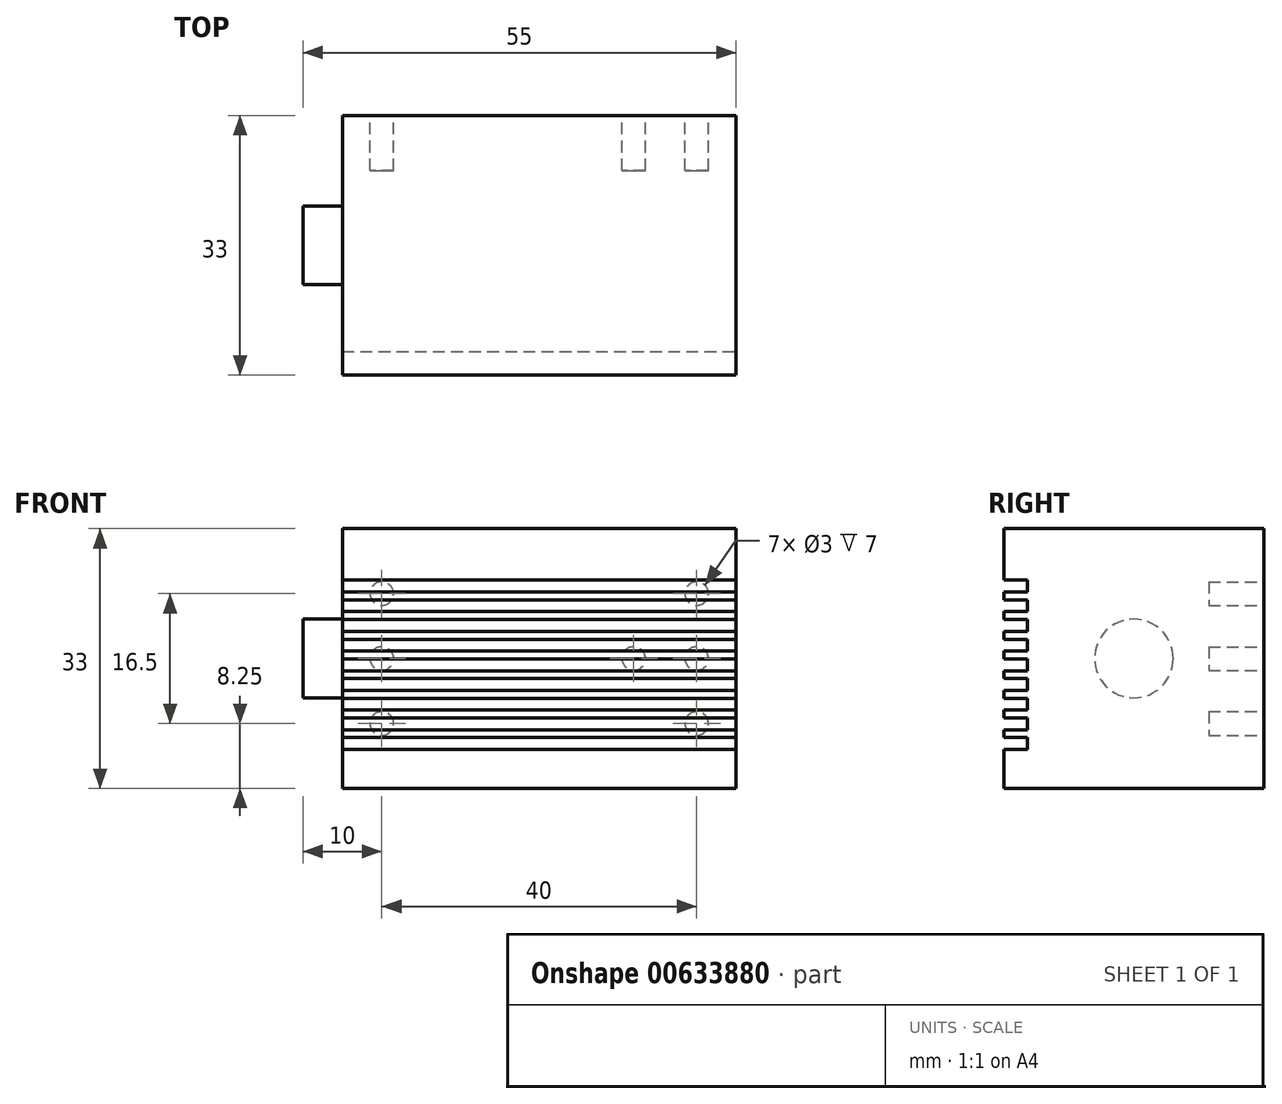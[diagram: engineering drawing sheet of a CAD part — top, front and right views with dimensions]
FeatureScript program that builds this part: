
annotation { "Feature Type Name" : "Feature", "Feature Type Description" : "" }
export const myFeature = defineFeature(function(context is Context, id is Id, definition is map)
    precondition{}
    {
        {
            var Q0;
            Q0=qCreatedBy(makeId("Top.planeOp"),FACE);
            var sketch = newSketch(context, id + "F0", { "sketchPlane" : qUnion([Q0])});
            skLineSegment(sketch, "E0.bottom", {"start": v(25, -16.5) * mm, "end": v(-25, -16.5) * mm});
            skLineSegment(sketch, "E0.top", {"start": v(25, 16.5) * mm, "end": v(-25, 16.5) * mm});
            skLineSegment(sketch, "E0.left", {"start": v(25, -16.5) * mm, "end": v(25, 16.5) * mm});
            skLineSegment(sketch, "E0.right", {"start": v(-25, -16.5) * mm, "end": v(-25, 16.5) * mm});
            skPoint(sketch, "E0.middle", {"position": v(0, 0) * mm});
            skSolve(sketch);
        }
        {
            var Q0;
            Q0=makeQuery(id+"F0.imprint","IMPRINT",FACE,{"disambiguationData":[TD([[makeQuery(id+"F0.imprint","IMPRINT",EDGE,{"derivedFrom":sQuery(id+"F0.wireOp",EDGE,"E0.bottom")}),-1.0]])]});
            extrude(context, id + "F1", {"entities" : qUnion([Q0]), "depth" : 33 * mm, "offsetDistance" : 25 * mm});
        }
        {
            var Q0;
            Q0=makeQuery(id+"F1.opExtrude","SWEPT_FACE",FACE,{"disambiguationData":[OSD([sQuery(id+"F0.wireOp",EDGE,"E0.left")])]});
            var sketch = newSketch(context, id + "F2", { "sketchPlane" : qUnion([Q0])});
            skLineSegment(sketch, "E1.bottom", {"start": v(-13.5, 24.95) * mm, "end": v(-19.5, 24.95) * mm});
            skLineSegment(sketch, "E1.top", {"start": v(-13.5, 26.45) * mm, "end": v(-19.5, 26.45) * mm});
            skLineSegment(sketch, "E1.left", {"start": v(-13.5, 24.95) * mm, "end": v(-13.5, 26.45) * mm});
            skLineSegment(sketch, "E1.right", {"start": v(-19.5, 24.95) * mm, "end": v(-19.5, 26.45) * mm});
            skPoint(sketch, "E1.middle", {"position": v(-16.5, 25.7) * mm});
            skPoint(sketch, "E2.0.1.0", {"position": v(-16.5, 23.2) * mm});
            skLineSegment(sketch, "E2.0.1.1", {"start": v(-13.5, 23.95) * mm, "end": v(-19.5, 23.95) * mm});
            skLineSegment(sketch, "E2.0.1.2", {"start": v(-13.5, 22.45) * mm, "end": v(-19.5, 22.45) * mm});
            skLineSegment(sketch, "E2.0.1.3", {"start": v(-19.5, 22.45) * mm, "end": v(-19.5, 23.95) * mm});
            skLineSegment(sketch, "E2.0.1.4", {"start": v(-13.5, 22.45) * mm, "end": v(-13.5, 23.95) * mm});
            skPoint(sketch, "E2.0.2.0", {"position": v(-16.5, 20.7) * mm});
            skLineSegment(sketch, "E2.0.2.1", {"start": v(-13.5, 21.45) * mm, "end": v(-19.5, 21.45) * mm});
            skLineSegment(sketch, "E2.0.2.2", {"start": v(-13.5, 19.95) * mm, "end": v(-19.5, 19.95) * mm});
            skLineSegment(sketch, "E2.0.2.3", {"start": v(-19.5, 19.95) * mm, "end": v(-19.5, 21.45) * mm});
            skLineSegment(sketch, "E2.0.2.4", {"start": v(-13.5, 19.95) * mm, "end": v(-13.5, 21.45) * mm});
            skPoint(sketch, "E2.0.3.0", {"position": v(-16.5, 18.2) * mm});
            skLineSegment(sketch, "E2.0.3.1", {"start": v(-13.5, 18.95) * mm, "end": v(-19.5, 18.95) * mm});
            skLineSegment(sketch, "E2.0.3.2", {"start": v(-13.5, 17.45) * mm, "end": v(-19.5, 17.45) * mm});
            skLineSegment(sketch, "E2.0.3.3", {"start": v(-19.5, 17.45) * mm, "end": v(-19.5, 18.95) * mm});
            skLineSegment(sketch, "E2.0.3.4", {"start": v(-13.5, 17.45) * mm, "end": v(-13.5, 18.95) * mm});
            skPoint(sketch, "E2.0.4.0", {"position": v(-16.5, 15.7) * mm});
            skLineSegment(sketch, "E2.0.4.1", {"start": v(-13.5, 16.45) * mm, "end": v(-19.5, 16.45) * mm});
            skLineSegment(sketch, "E2.0.4.2", {"start": v(-13.5, 14.95) * mm, "end": v(-19.5, 14.95) * mm});
            skLineSegment(sketch, "E2.0.4.3", {"start": v(-19.5, 14.95) * mm, "end": v(-19.5, 16.45) * mm});
            skLineSegment(sketch, "E2.0.4.4", {"start": v(-13.5, 14.95) * mm, "end": v(-13.5, 16.45) * mm});
            skPoint(sketch, "E2.0.5.0", {"position": v(-16.5, 13.2) * mm});
            skLineSegment(sketch, "E2.0.5.1", {"start": v(-13.5, 13.95) * mm, "end": v(-19.5, 13.95) * mm});
            skLineSegment(sketch, "E2.0.5.2", {"start": v(-13.5, 12.45) * mm, "end": v(-19.5, 12.45) * mm});
            skLineSegment(sketch, "E2.0.5.3", {"start": v(-19.5, 12.45) * mm, "end": v(-19.5, 13.95) * mm});
            skLineSegment(sketch, "E2.0.5.4", {"start": v(-13.5, 12.45) * mm, "end": v(-13.5, 13.95) * mm});
            skPoint(sketch, "E2.0.6.0", {"position": v(-16.5, 10.7) * mm});
            skLineSegment(sketch, "E2.0.6.1", {"start": v(-13.5, 11.45) * mm, "end": v(-19.5, 11.45) * mm});
            skLineSegment(sketch, "E2.0.6.2", {"start": v(-13.5, 9.95) * mm, "end": v(-19.5, 9.95) * mm});
            skLineSegment(sketch, "E2.0.6.3", {"start": v(-19.5, 9.95) * mm, "end": v(-19.5, 11.45) * mm});
            skLineSegment(sketch, "E2.0.6.4", {"start": v(-13.5, 9.95) * mm, "end": v(-13.5, 11.45) * mm});
            skPoint(sketch, "E2.0.7.0", {"position": v(-16.5, 8.2) * mm});
            skLineSegment(sketch, "E2.0.7.1", {"start": v(-13.5, 8.95) * mm, "end": v(-19.5, 8.95) * mm});
            skLineSegment(sketch, "E2.0.7.2", {"start": v(-13.5, 7.45) * mm, "end": v(-19.5, 7.45) * mm});
            skLineSegment(sketch, "E2.0.7.3", {"start": v(-19.5, 7.45) * mm, "end": v(-19.5, 8.95) * mm});
            skLineSegment(sketch, "E2.0.7.4", {"start": v(-13.5, 7.45) * mm, "end": v(-13.5, 8.95) * mm});
            skPoint(sketch, "E2.0.8.0", {"position": v(-16.5, 5.7) * mm});
            skLineSegment(sketch, "E2.0.8.1", {"start": v(-13.5, 6.45) * mm, "end": v(-19.5, 6.45) * mm});
            skLineSegment(sketch, "E2.0.8.2", {"start": v(-13.5, 4.95) * mm, "end": v(-19.5, 4.95) * mm});
            skLineSegment(sketch, "E2.0.8.3", {"start": v(-19.5, 4.95) * mm, "end": v(-19.5, 6.45) * mm});
            skLineSegment(sketch, "E2.0.8.4", {"start": v(-13.5, 4.95) * mm, "end": v(-13.5, 6.45) * mm});
            skLineSegment(sketch, "E2.direction1", {"start": v(-19.5, 24.95) * mm, "end": v(5.5, 24.95) * mm, "construction": true});
            skLineSegment(sketch, "E2.direction2", {"start": v(-19.5, 24.95) * mm, "end": v(-19.5, 22.45) * mm, "construction": true});
            skSolve(sketch);
        }
        {
            var Q0;
            Q0 = qSketchRegion(id + "F2", true);
            extrude(context, id + "F3", {"entities" : qUnion([Q0]), "operationType" : NewBodyOperationType.REMOVE, "endBound" : BoundingType.THROUGH_ALL, "oppositeDirection" : true, "depth" : 25 * mm, "offsetDistance" : 25 * mm});
        }
        {
            var Q0;
            Q0=makeQuery(id+"F1.opExtrude","SWEPT_FACE",FACE,{"disambiguationData":[OSD([sQuery(id+"F0.wireOp",EDGE,"E0.right")])]});
            var sketch = newSketch(context, id + "F4", { "sketchPlane" : qUnion([Q0])});
            skCircle(sketch, "E3", {"center": v(0, 16.5) * mm, "radius": 5 * mm});
            skPoint(sketch, "E3.centerSnap0", {"position": v(-16.5, 16.5) * mm});
            skSolve(sketch);
        }
        {
            var Q0;
            Q0=makeQuery(id+"F4.imprint","IMPRINT",FACE,{"disambiguationData":[TD([[makeQuery(id+"F4.imprint","IMPRINT",EDGE,{"derivedFrom":sQuery(id+"F4.wireOp",EDGE,"E3")}),1.0]])]});
            extrude(context, id + "F5", {"entities" : qUnion([Q0]), "operationType" : NewBodyOperationType.ADD, "depth" : 5 * mm, "offsetDistance" : 25 * mm});
        }
        {
            var Q0;
            Q0=makeQuery(id+"F1.opExtrude","SWEPT_FACE",FACE,{"disambiguationData":[OSD([sQuery(id+"F0.wireOp",EDGE,"E0.top")])]});
            var sketch = newSketch(context, id + "F6", { "sketchPlane" : qUnion([Q0])});
            skCircle(sketch, "E4", {"center": v(-20, 8.25) * mm, "radius": 1.5 * mm});
            skCircle(sketch, "E5", {"center": v(-20, 16.5) * mm, "radius": 1.5 * mm});
            skCircle(sketch, "E6", {"center": v(-20, 24.75) * mm, "radius": 1.5 * mm});
            skCircle(sketch, "E7", {"center": v(-12, 16.5) * mm, "radius": 1.5 * mm});
            skCircle(sketch, "E8", {"center": v(20, 16.5) * mm, "radius": 1.5 * mm});
            skCircle(sketch, "E9.MirrorC", {"center": v(20, 8.25) * mm, "radius": 1.5 * mm});
            skCircle(sketch, "E10.MirrorC", {"center": v(20, 24.75) * mm, "radius": 1.5 * mm});
            skSolve(sketch);
        }
        {
            var Q0;
            Q0 = qSketchRegion(id + "F6", true);
            extrude(context, id + "F7", {"entities" : qUnion([Q0]), "operationType" : NewBodyOperationType.REMOVE, "oppositeDirection" : true, "depth" : 7 * mm, "offsetDistance" : 25 * mm});
        }
    });
